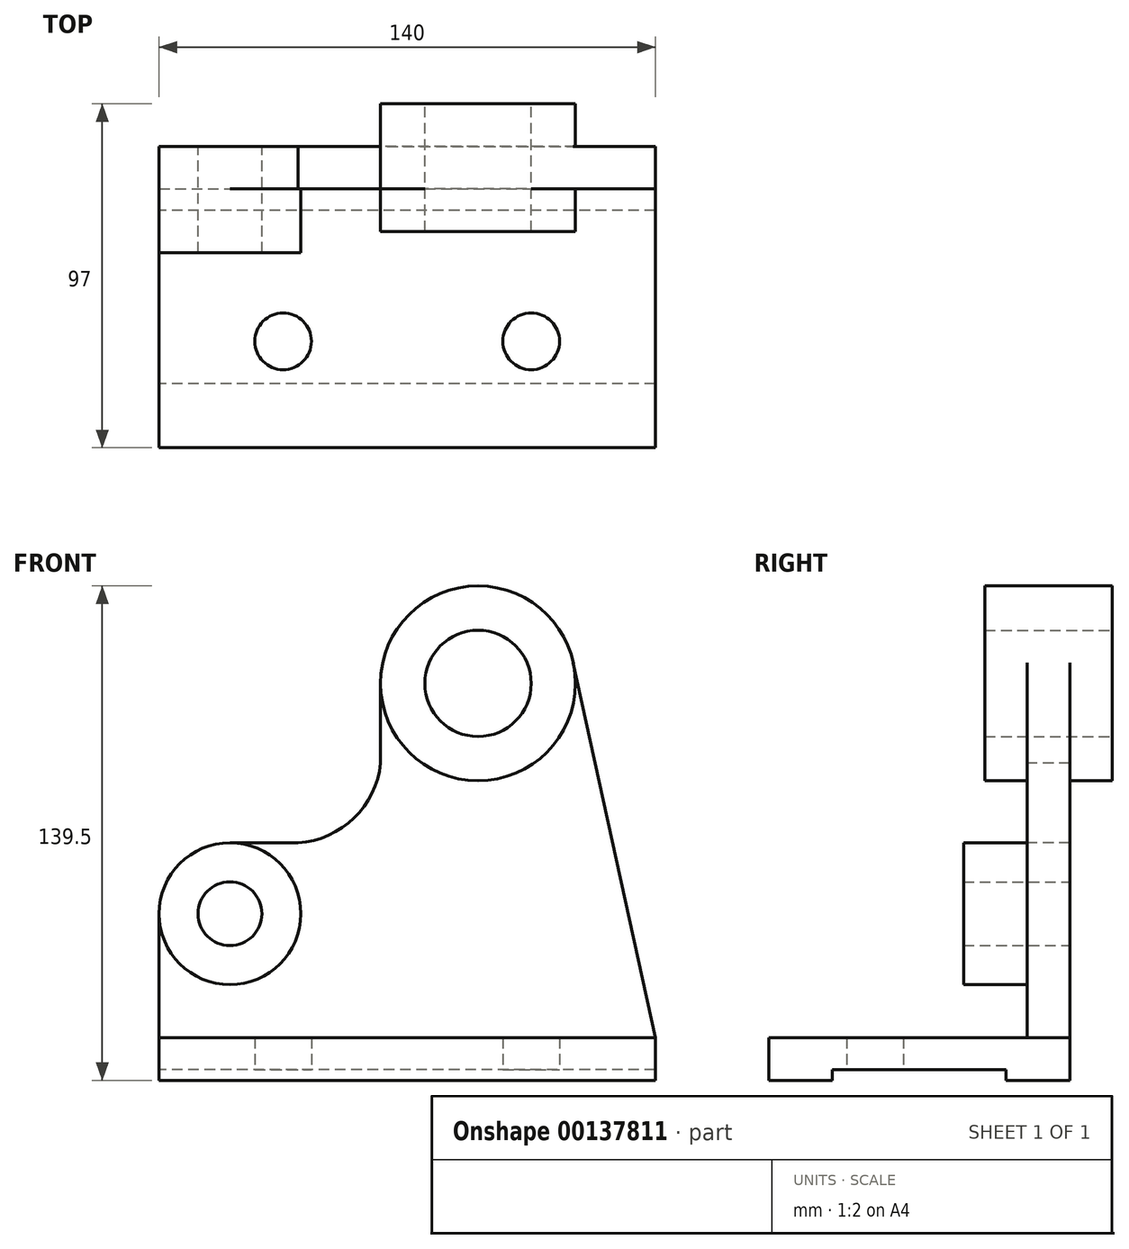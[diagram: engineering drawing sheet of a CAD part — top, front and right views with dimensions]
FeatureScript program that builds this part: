
annotation { "Feature Type Name" : "Feature", "Feature Type Description" : "" }
export const myFeature = defineFeature(function(context is Context, id is Id, definition is map)
    precondition{}
    {
        {
            var Q0;
            Q0=qCreatedBy(makeId("Top.planeOp"),FACE);
            var sketch = newSketch(context, id + "F0", { "sketchPlane" : qUnion([Q0])});
            skLineSegment(sketch, "E0.bottom", {"start": v(0, 0) * mm, "end": v(140, 0) * mm});
            skLineSegment(sketch, "E0.top", {"start": v(0, 85) * mm, "end": v(140, 85) * mm});
            skLineSegment(sketch, "E0.left", {"start": v(0, 0) * mm, "end": v(0, 85) * mm});
            skLineSegment(sketch, "E0.right", {"start": v(140, 0) * mm, "end": v(140, 85) * mm});
            skCircle(sketch, "E1", {"center": v(105, 30) * mm, "radius": 8 * mm});
            skCircle(sketch, "E2", {"center": v(35, 30) * mm, "radius": 8 * mm});
            skSolve(sketch);
        }
        {
            var Q0;
            Q0=makeQuery(id+"F0.imprint","IMPRINT",FACE,{"disambiguationData":[TD([[makeQuery(id+"F0.imprint","IMPRINT",EDGE,{"derivedFrom":sQuery(id+"F0.wireOp",EDGE,"E0.bottom")}),1.0]])]});
            extrude(context, id + "F1", {"entities" : qUnion([Q0]), "depth" : 12 * mm});
        }
        {
            var Q0;
            Q0=makeQuery(id+"F1.opExtrude","CAP_FACE",FACE,{"disambiguationData":[OSD([sQuery(id+"F0.wireOp",EDGE,"E0.bottom"),sQuery(id+"F0.wireOp",EDGE,"E0.top"),sQuery(id+"F0.wireOp",EDGE,"E0.left"),sQuery(id+"F0.wireOp",EDGE,"E0.right"),sQuery(id+"F0.wireOp",EDGE,"E1"),sQuery(id+"F0.wireOp",EDGE,"E2")])],"isStart":false});
            var sketch = newSketch(context, id + "F2", { "sketchPlane" : qUnion([Q0])});
            skLineSegment(sketch, "E3.bottom", {"start": v(0, 85) * mm, "end": v(140, 85) * mm});
            skLineSegment(sketch, "E3.top", {"start": v(0, 73) * mm, "end": v(140, 73) * mm});
            skLineSegment(sketch, "E3.left", {"start": v(0, 85) * mm, "end": v(0, 73) * mm});
            skLineSegment(sketch, "E3.right", {"start": v(140, 85) * mm, "end": v(140, 73) * mm});
            skSolve(sketch);
        }
        {
            var Q0;
            Q0=makeQuery(id+"F2.imprint","IMPRINT",FACE,{"disambiguationData":[TD([[makeQuery(id+"F2.imprint","IMPRINT",EDGE,{"derivedFrom":sQuery(id+"F2.wireOp",EDGE,"E3.bottom")}),-1.0]])]});
            extrude(context, id + "F3", {"entities" : qUnion([Q0]), "operationType" : NewBodyOperationType.ADD, "depth" : 130 * mm});
        }
        {
            var Q0;
            Q0=makeQuery(id+"F3.opExtrude","SWEPT_FACE",FACE,{"disambiguationData":[OSD([sQuery(id+"F2.wireOp",EDGE,"E3.top")])]});
            var sketch = newSketch(context, id + "F4", { "sketchPlane" : qUnion([Q0])});
            skLineSegment(sketch, "E4", {"start": v(0, 12) * mm, "end": v(20, 12) * mm});
            skLineSegment(sketch, "E5", {"start": v(20, 12) * mm, "end": v(20, 47) * mm});
            skCircle(sketch, "E6", {"center": v(20, 47) * mm, "radius": 20 * mm});
            skCircle(sketch, "E7", {"center": v(20, 47) * mm, "radius": 9 * mm});
            skSolve(sketch);
        }
        {
            var Q0;
            Q0=makeQuery(id+"F4.imprint","IMPRINT",FACE,{"disambiguationData":[TD([[makeQuery(id+"F4.imprint","IMPRINT",EDGE,{"derivedFrom":sQuery(id+"F4.wireOp",EDGE,"E7")}),-1.0]])]});
            extrude(context, id + "F5", {"entities" : qUnion([Q0]), "operationType" : NewBodyOperationType.ADD, "depth" : 18 * mm});
        }
        {
            var Q0;
            {var subQ2=sQuery(id+"F2.wireOp",EDGE,"E3.top");var subQ4=sQuery(id+"F0.wireOp",EDGE,"E0.left");Q0=makeQuery(id+"F5.boolean.opBoolean","SPLIT",FACE,{"disambiguationData":[TD([makeQuery(id+"F1.opExtrude","SWEPT_FACE",FACE,{"disambiguationData":[OSD([subQ4])]})])],"derivedFrom":makeQuery(id+"F3.opExtrude","SWEPT_FACE",FACE,{"disambiguationData":[OSD([subQ2])]})});}
            var sketch = newSketch(context, id + "F6", { "sketchPlane" : qUnion([Q0])});
            skLineSegment(sketch, "E8", {"start": v(140, 12) * mm, "end": v(90, 12) * mm});
            skLineSegment(sketch, "E9", {"start": v(90, 12) * mm, "end": v(90, 112) * mm});
            skCircle(sketch, "E10", {"center": v(90, 112) * mm, "radius": 27.5 * mm});
            skCircle(sketch, "E11", {"center": v(90, 112) * mm, "radius": 15 * mm});
            skSolve(sketch);
        }
        {
            var Q0;
            Q0=makeQuery(id+"F6.imprint","IMPRINT",FACE,{"disambiguationData":[TD([[makeQuery(id+"F6.imprint","IMPRINT",EDGE,{"derivedFrom":sQuery(id+"F6.wireOp",EDGE,"E10")}),1.0]])]});
            extrude(context, id + "F7", {"entities" : qUnion([Q0]), "operationType" : NewBodyOperationType.ADD, "depth" : 12 * mm});
        }
        {
            var Q0;
            {var subQ2=sQuery(id+"F2.wireOp",EDGE,"E3.top");var subQ6=sQuery(id+"F0.wireOp",EDGE,"E0.left");var subQ7=makeQuery(id+"F1.opExtrude","SWEPT_FACE",FACE,{"disambiguationData":[OSD([subQ6])]});Q0=makeQuery(id+"F7.boolean.opBoolean","SPLIT",FACE,{"disambiguationData":[TD([subQ7])],"derivedFrom":makeQuery(id+"F5.boolean.opBoolean","SPLIT",FACE,{"disambiguationData":[TD([subQ7])],"derivedFrom":makeQuery(id+"F3.opExtrude","SWEPT_FACE",FACE,{"disambiguationData":[OSD([subQ2])]})})});}
            var sketch = newSketch(context, id + "F8", { "sketchPlane" : qUnion([Q0])});
            skLineSegment(sketch, "E12", {"start": v(62.5, 112) * mm, "end": v(62.5, 89.5) * mm});
            skLineSegment(sketch, "E13", {"start": v(20, 67) * mm, "end": v(39.26, 67) * mm});
            skPoint(sketch, "E14.start.orphan", {"position": v(90, 112) * mm});
            skPoint(sketch, "E15.start.orphan", {"position": v(20, 47) * mm});
            skArc(sketch, "E16", {"start": v(35.98, 67) * mm, "mid": v(53.8, 72.88) * mm, "end": v(62.5, 89.5) * mm});
            skPoint(sketch, "E17.orphan", {"position": v(62.5, 67) * mm});
            skLineSegment(sketch, "E18", {"start": v(140, 12) * mm, "end": v(116.87, 117.87) * mm});
            skSolve(sketch);
        }
        {
            var Q0;
            {var subQ1=sQuery(id+"F8.wireOp",EDGE,"E12");Q0=makeQuery(id+"F8.imprint","IMPRINT",FACE,{"disambiguationData":[TD([[makeQuery(id+"F8.imprint","IMPRINT",EDGE,{"derivedFrom":subQ1}),-1.0]])]});}
            extrude(context, id + "F9", {"entities" : qUnion([Q0]), "operationType" : NewBodyOperationType.REMOVE, "oppositeDirection" : true, "depth" : 25 * mm});
        }
        {
            var Q0;
            {var subQ2=sQuery(id+"F2.wireOp",EDGE,"E3.top");var subQ4=sQuery(id+"F0.wireOp",EDGE,"E0.left");Q0=makeQuery(id+"F7.boolean.opBoolean","SPLIT",FACE,{"disambiguationData":[TD([makeQuery(id+"F7.opExtrude","SWEPT_FACE",FACE,{"disambiguationData":[OSD([sQuery(id+"F6.wireOp",EDGE,"E11")])]})])],"derivedFrom":makeQuery(id+"F5.boolean.opBoolean","SPLIT",FACE,{"disambiguationData":[TD([makeQuery(id+"F1.opExtrude","SWEPT_FACE",FACE,{"disambiguationData":[OSD([subQ4])]})])],"derivedFrom":makeQuery(id+"F3.opExtrude","SWEPT_FACE",FACE,{"disambiguationData":[OSD([subQ2])]})})});}
            var Q1;
            Q1=makeQuery(id+"F5.boolean.opBoolean","SPLIT",FACE,{"disambiguationData":[TD([makeQuery(id+"F5.opExtrude","SWEPT_FACE",FACE,{"disambiguationData":[OSD([sQuery(id+"F4.wireOp",EDGE,"E7")])]})])],"derivedFrom":makeQuery(id+"F3.opExtrude","SWEPT_FACE",FACE,{"disambiguationData":[OSD([sQuery(id+"F2.wireOp",EDGE,"E3.top")])]})});
            extrude(context, id + "F10", {"entities" : qUnion([Q0, Q1]), "operationType" : NewBodyOperationType.REMOVE, "oppositeDirection" : true, "depth" : 25 * mm});
        }
        {
            var Q0;
            Q0=makeQuery(id+"F3.boolean.opBoolean","MERGE",FACE,{"derivedFrom":[makeQuery(id+"F1.opExtrude","SWEPT_FACE",FACE,{"disambiguationData":[OSD([sQuery(id+"F0.wireOp",EDGE,"E0.left")])]}),makeQuery(id+"F3.opExtrude","SWEPT_FACE",FACE,{"disambiguationData":[OSD([sQuery(id+"F2.wireOp",EDGE,"E3.left")])]})]});
            var sketch = newSketch(context, id + "F11", { "sketchPlane" : qUnion([Q0])});
            skLineSegment(sketch, "E19.bottom", {"start": v(-67, 0) * mm, "end": v(-18, 0) * mm});
            skLineSegment(sketch, "E19.top", {"start": v(-67, 3) * mm, "end": v(-18, 3) * mm});
            skLineSegment(sketch, "E19.left", {"start": v(-67, 0) * mm, "end": v(-67, 3) * mm});
            skLineSegment(sketch, "E19.right", {"start": v(-18, 0) * mm, "end": v(-18, 3) * mm});
            skSolve(sketch);
        }
        {
            var Q0;
            Q0=makeQuery(id+"F11.imprint","IMPRINT",FACE,{"disambiguationData":[TD([[makeQuery(id+"F11.imprint","IMPRINT",EDGE,{"derivedFrom":sQuery(id+"F11.wireOp",EDGE,"E19.bottom")}),-1.0]])]});
            extrude(context, id + "F12", {"entities" : qUnion([Q0]), "operationType" : NewBodyOperationType.REMOVE, "endBound" : BoundingType.THROUGH_ALL, "oppositeDirection" : true, "depth" : 25 * mm});
        }
        {
            var Q0;
            Q0=makeQuery(id+"F3.boolean.opBoolean","MERGE",FACE,{"derivedFrom":[makeQuery(id+"F1.opExtrude","SWEPT_FACE",FACE,{"disambiguationData":[OSD([sQuery(id+"F0.wireOp",EDGE,"E0.top")])]}),makeQuery(id+"F3.opExtrude","SWEPT_FACE",FACE,{"disambiguationData":[OSD([sQuery(id+"F2.wireOp",EDGE,"E3.bottom")])]})]});
            var sketch = newSketch(context, id + "F13", { "sketchPlane" : qUnion([Q0])});
            skCircle(sketch, "E20", {"center": v(-90, 112) * mm, "radius": 27.5 * mm});
            skCircle(sketch, "E21", {"center": v(-90, 112) * mm, "radius": 15 * mm});
            skSolve(sketch);
        }
        {
            var Q0;
            Q0=makeQuery(id+"F13.imprint","IMPRINT",FACE,{"disambiguationData":[TD([[makeQuery(id+"F13.imprint","IMPRINT",EDGE,{"derivedFrom":sQuery(id+"F13.wireOp",EDGE,"E21")}),-1.0]])]});
            extrude(context, id + "F14", {"entities" : qUnion([Q0]), "operationType" : NewBodyOperationType.ADD, "depth" : 12 * mm});
        }
    });
